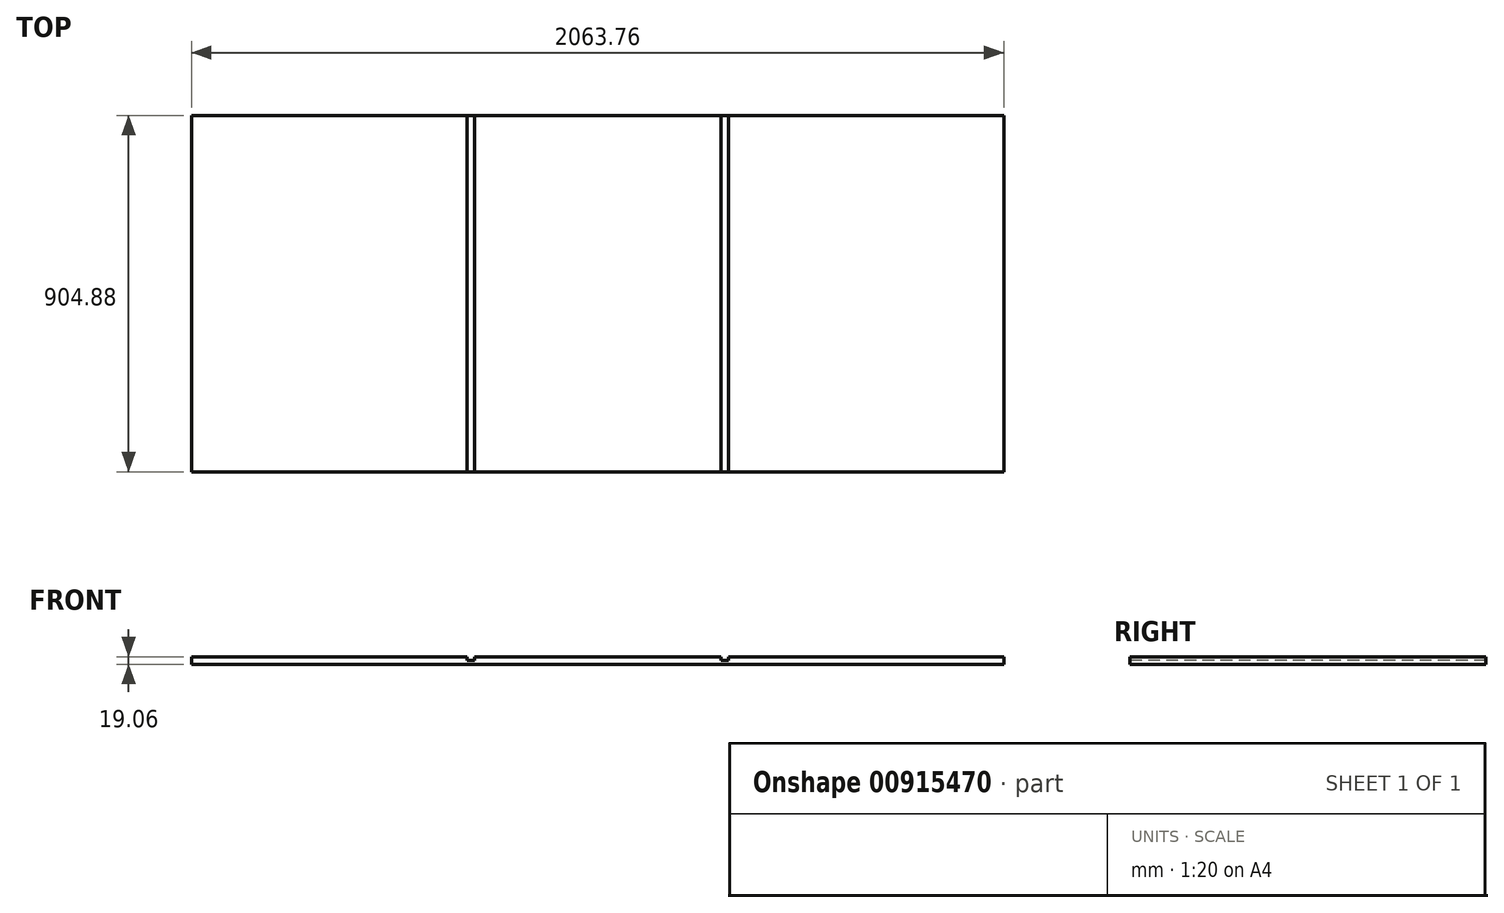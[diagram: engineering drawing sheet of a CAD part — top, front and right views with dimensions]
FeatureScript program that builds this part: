
annotation { "Feature Type Name" : "Feature", "Feature Type Description" : "" }
export const myFeature = defineFeature(function(context is Context, id is Id, definition is map)
    precondition{}
    {
        {
            var Q0;
            Q0=qCreatedBy(makeId("Top.planeOp"),FACE);
            var sketch = newSketch(context, id + "F0", { "sketchPlane" : qUnion([Q0])});
            skLineSegment(sketch, "E0.bottom", {"start": v(1031.88, 452.44) * mm, "end": v(-1031.88, 452.44) * mm});
            skLineSegment(sketch, "E0.top", {"start": v(1031.88, -452.44) * mm, "end": v(-1031.88, -452.44) * mm});
            skLineSegment(sketch, "E0.left", {"start": v(1031.88, 452.44) * mm, "end": v(1031.88, -452.44) * mm});
            skLineSegment(sketch, "E0.right", {"start": v(-1031.88, 452.44) * mm, "end": v(-1031.88, -452.44) * mm});
            skPoint(sketch, "E0.middle", {"position": v(0, 0) * mm});
            skSolve(sketch);
        }
        {
            var Q0;
            Q0=qCreatedBy(makeId("Top.planeOp"),FACE);
            var sketch = newSketch(context, id + "F1", { "sketchPlane" : qUnion([Q0])});
            skLineSegment(sketch, "E1.bottom", {"start": v(-1031.88, 452.44) * mm, "end": v(-332.32, 452.44) * mm});
            skLineSegment(sketch, "E1.top", {"start": v(-1031.88, -452.44) * mm, "end": v(-332.32, -452.44) * mm});
            skLineSegment(sketch, "E1.left", {"start": v(-1031.88, 452.44) * mm, "end": v(-1031.88, -452.44) * mm});
            skLineSegment(sketch, "E1.right", {"start": v(1031.88, 452.44) * mm, "end": v(1031.88, -452.44) * mm});
            skPoint(sketch, "E1.middle", {"position": v(0, 0) * mm});
            skLineSegment(sketch, "E2", {"start": v(313.27, 452.44) * mm, "end": v(313.27, -452.44) * mm});
            skLineSegment(sketch, "E3", {"start": v(332.32, 452.44) * mm, "end": v(332.32, -452.44) * mm});
            skLineSegment(sketch, "E4.trimOffspring", {"start": v(332.32, -452.44) * mm, "end": v(1031.88, -452.44) * mm});
            skLineSegment(sketch, "E5.trimOffspring", {"start": v(332.32, 452.44) * mm, "end": v(1031.88, 452.44) * mm});
            skLineSegment(sketch, "E6", {"start": v(-332.32, 452.44) * mm, "end": v(-332.32, -452.44) * mm});
            skLineSegment(sketch, "E7", {"start": v(-313.27, 452.44) * mm, "end": v(-313.27, -452.44) * mm});
            skLineSegment(sketch, "E8.trimOffspring", {"start": v(-313.27, 452.44) * mm, "end": v(313.27, 452.44) * mm});
            skLineSegment(sketch, "E9.trimOffspring", {"start": v(-313.27, -452.44) * mm, "end": v(313.27, -452.44) * mm});
            skSolve(sketch);
        }
        {
            var Q0;
            Q0=qSketchRegion(id+"F0",true);
            extrude(context, id + "F2", {"entities" : qUnion([Q0]), "oppositeDirection" : true, "depth" : 9.52 * mm, "offsetDistance" : 25.4 * mm});
        }
        {
            var Q0;
            Q0=qSketchRegion(id+"F1",true);
            extrude(context, id + "F3", {"entities" : qUnion([Q0]), "operationType" : NewBodyOperationType.ADD, "depth" : 9.52 * mm, "offsetDistance" : 25.4 * mm});
        }
    });
